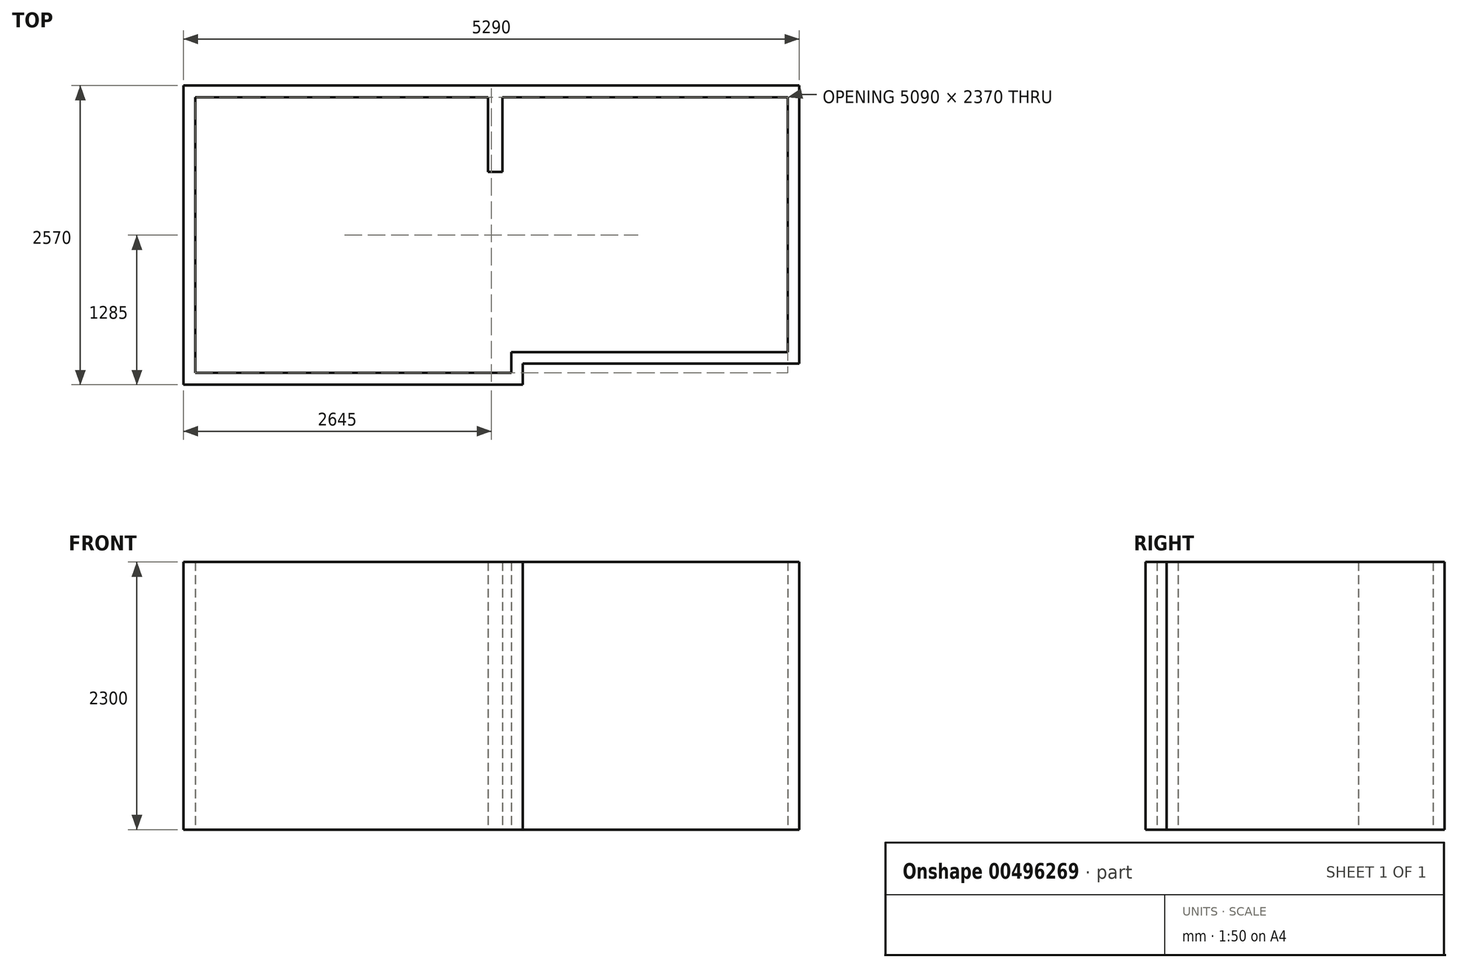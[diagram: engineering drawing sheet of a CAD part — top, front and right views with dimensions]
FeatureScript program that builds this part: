
annotation { "Feature Type Name" : "Feature", "Feature Type Description" : "" }
export const myFeature = defineFeature(function(context is Context, id is Id, definition is map)
    precondition{}
    {
        {
            var Q0;
            Q0=qCreatedBy(makeId("Top.planeOp"),FACE);
            var sketch = newSketch(context, id + "F0", { "sketchPlane" : qUnion([Q0])});
            skLineSegment(sketch, "E0", {"start": v(0, 0) * mm, "end": v(0, 2370) * mm});
            skLineSegment(sketch, "E1", {"start": v(0, 2370) * mm, "end": v(2515, 2370) * mm});
            skLineSegment(sketch, "E2", {"start": v(2515, 2370) * mm, "end": v(2515, 1730) * mm});
            skLineSegment(sketch, "E3", {"start": v(2515, 1730) * mm, "end": v(2640, 1730) * mm});
            skLineSegment(sketch, "E4", {"start": v(2640, 1730) * mm, "end": v(2640, 2370) * mm});
            skLineSegment(sketch, "E5", {"start": v(2640, 2370) * mm, "end": v(5090, 2370) * mm});
            skLineSegment(sketch, "E6", {"start": v(5090, 2370) * mm, "end": v(5090, 180) * mm});
            skLineSegment(sketch, "E7", {"start": v(0, 0) * mm, "end": v(2715, 0) * mm});
            skLineSegment(sketch, "E8", {"start": v(2715, 0) * mm, "end": v(2715, 180) * mm});
            skLineSegment(sketch, "E9", {"start": v(2715, 180) * mm, "end": v(5090, 180) * mm});
            skLineSegment(sketch, "E10.0", {"start": v(2815, 80) * mm, "end": v(5190, 80) * mm});
            skLineSegment(sketch, "E10.1", {"start": v(5190, 2470) * mm, "end": v(5190, 80) * mm});
            skLineSegment(sketch, "E10.2", {"start": v(-100, -100) * mm, "end": v(2515, -100) * mm});
            skLineSegment(sketch, "E10.3", {"start": v(-100, -100) * mm, "end": v(-100, 2470) * mm});
            skLineSegment(sketch, "E10.4", {"start": v(-100, 2470) * mm, "end": v(2610, 2470) * mm});
            skLineSegment(sketch, "E10.5", {"start": v(2610, 2470) * mm, "end": v(5190, 2470) * mm});
            skLineSegment(sketch, "E11", {"start": v(2515, -100) * mm, "end": v(2815, -100) * mm});
            skLineSegment(sketch, "E12", {"start": v(2815, -100) * mm, "end": v(2815, 80) * mm});
            skSolve(sketch);
        }
        {
            var Q0;
            Q0=makeQuery(id+"F0.imprint","IMPRINT",FACE,{"disambiguationData":[TD([[makeQuery(id+"F0.imprint","IMPRINT",EDGE,{"derivedFrom":sQuery(id+"F0.wireOp",EDGE,"E0")}),1.0]])]});
            extrude(context, id + "F1", {"entities" : qUnion([Q0]), "depth" : 2300 * mm});
        }
    });
